# Revit family: Zumtobel basicDIM ILD G2 SSM 20 4DPI WDA
name_source: partatom
category: Lighting Devices
units: mm (PartAtom-declared; Revit-internal decimal feet)

## family parameters
Cut with Voids When Loaded = Yes
Host = Face
Maintain Annotation Orientation = No
OmniClass Number = 23.85.80.11.27
OmniClass Title = Lighting Controls
Part Type = Normal
Room Calculation Point = Yes
Round Connector Dimension = Use Diameter
Shared = No

## types (1)
- basicDIM ILD G2 SSM 20 4DPI WDA WH
    Assembly Code = D5030800
    Default Elevation = 0 mm  [stored 0 ft]
    Description = Motion Sensor
    Manufacturer = Zumtobel Lighting
    Material-Housing = ZG-Lighting Fixtures-Plastic-White_RGB 255 255 255
    Model = 28004640
    Type Image = basicDIM ILD G2 SSM 20 4DPI WDA WH.jpg
    URL = https://www.zumtobel.com

note: [stored X ft] marks values corroborated as IEEE doubles in the binary element streams (Revit-internal decimal feet)

## geometry (parser evidence)
native form markers: Sweep x2
no freeform markers — native parametric forms only
